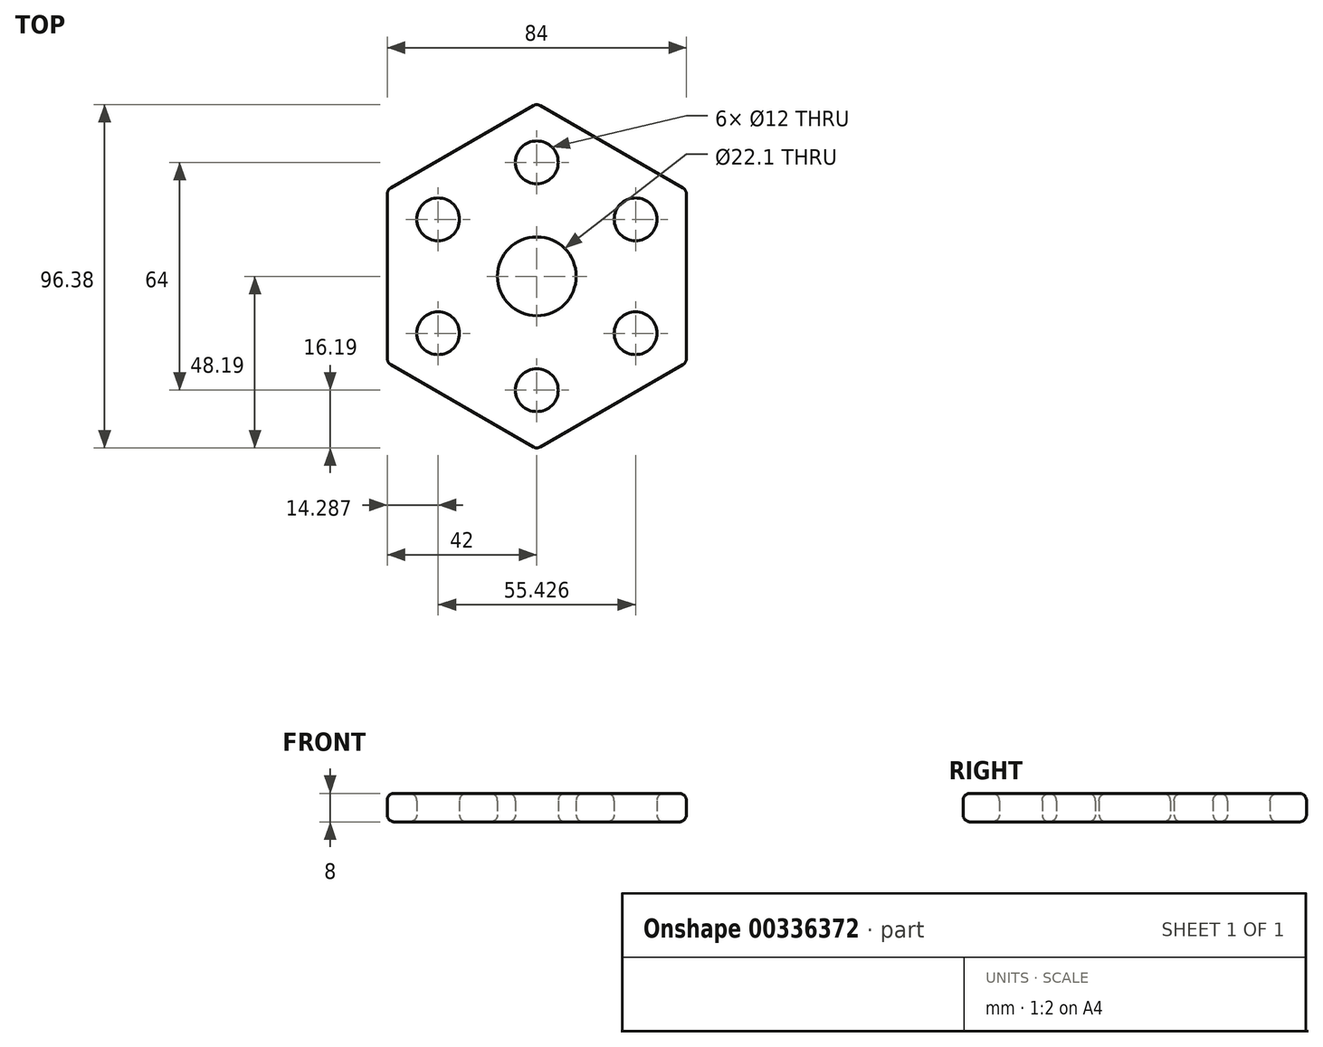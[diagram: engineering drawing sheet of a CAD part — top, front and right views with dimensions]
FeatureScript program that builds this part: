
annotation { "Feature Type Name" : "Feature", "Feature Type Description" : "" }
export const myFeature = defineFeature(function(context is Context, id is Id, definition is map)
    precondition{}
    {
        {
            var Q0;
            Q0=qCreatedBy(makeId("Top.planeOp"),FACE);
            var sketch = newSketch(context, id + "F0", { "sketchPlane" : qUnion([Q0])});
            skCircle(sketch, "E0", {"center": v(0, 0) * mm, "radius": 11.05 * mm});
            skLineSegment(sketch, "E1.0", {"start": v(-42, -24.25) * mm, "end": v(-42, 24.25) * mm});
            skLineSegment(sketch, "E1.1", {"start": v(-42, 24.25) * mm, "end": v(0, 48.5) * mm});
            skLineSegment(sketch, "E1.2", {"start": v(0, 48.5) * mm, "end": v(42, 24.25) * mm});
            skLineSegment(sketch, "E1.3", {"start": v(42, 24.25) * mm, "end": v(42, -24.25) * mm});
            skLineSegment(sketch, "E1.4", {"start": v(42, -24.25) * mm, "end": v(0, -48.5) * mm});
            skLineSegment(sketch, "E1.5", {"start": v(0, -48.5) * mm, "end": v(-42, -24.25) * mm});
            skPoint(sketch, "E1.0.midPoint", {"position": v(-42, 0) * mm});
            skCircle(sketch, "E2", {"center": v(-27.71, 16) * mm, "radius": 6 * mm});
            skCircle(sketch, "E3.MirrorC", {"center": v(-27.71, -16) * mm, "radius": 6 * mm});
            skCircle(sketch, "E4.MirrorC", {"center": v(27.71, 16) * mm, "radius": 6 * mm});
            skCircle(sketch, "E5.MirrorC", {"center": v(27.71, -16) * mm, "radius": 6 * mm});
            skCircle(sketch, "E6.MirrorC", {"center": v(0, 32) * mm, "radius": 6 * mm});
            skCircle(sketch, "E7.MirrorC", {"center": v(0, -32) * mm, "radius": 6 * mm});
            skPoint(sketch, "E8.end.orphan", {"position": v(21, 36.37) * mm});
            skSolve(sketch);
        }
        {
            var Q0;
            Q0 = qSketchRegion(id + "F0", true);
            extrude(context, id + "F1", {"entities" : qUnion([Q0]), "depth" : 8 * mm, "offsetDistance" : 25 * mm});
        }
        {
            var Q0;
            Q0=makeQuery(id+"F1.opExtrude","CAP_FACE",FACE,{"disambiguationData":[OSD([sQuery(id+"F0.wireOp",EDGE,"E0"),sQuery(id+"F0.wireOp",EDGE,"E1.0"),sQuery(id+"F0.wireOp",EDGE,"E1.1"),sQuery(id+"F0.wireOp",EDGE,"E1.2"),sQuery(id+"F0.wireOp",EDGE,"E1.3"),sQuery(id+"F0.wireOp",EDGE,"E1.4"),sQuery(id+"F0.wireOp",EDGE,"E1.5"),sQuery(id+"F0.wireOp",EDGE,"E2"),sQuery(id+"F0.wireOp",EDGE,"E3.MirrorC"),sQuery(id+"F0.wireOp",EDGE,"E4.MirrorC"),sQuery(id+"F0.wireOp",EDGE,"E5.MirrorC"),sQuery(id+"F0.wireOp",EDGE,"E6.MirrorC"),sQuery(id+"F0.wireOp",EDGE,"E7.MirrorC")])],"isStart":false});
            var Q1;
            Q1=makeQuery(id+"F1.opExtrude","CAP_FACE",FACE,{"disambiguationData":[OSD([sQuery(id+"F0.wireOp",EDGE,"E0"),sQuery(id+"F0.wireOp",EDGE,"E1.0"),sQuery(id+"F0.wireOp",EDGE,"E1.1"),sQuery(id+"F0.wireOp",EDGE,"E1.2"),sQuery(id+"F0.wireOp",EDGE,"E1.3"),sQuery(id+"F0.wireOp",EDGE,"E1.4"),sQuery(id+"F0.wireOp",EDGE,"E1.5"),sQuery(id+"F0.wireOp",EDGE,"E2"),sQuery(id+"F0.wireOp",EDGE,"E3.MirrorC"),sQuery(id+"F0.wireOp",EDGE,"E4.MirrorC"),sQuery(id+"F0.wireOp",EDGE,"E5.MirrorC"),sQuery(id+"F0.wireOp",EDGE,"E6.MirrorC"),sQuery(id+"F0.wireOp",EDGE,"E7.MirrorC")])],"isStart":true});
            var Q2;
            Q2=makeQuery(id+"F1.opExtrude","SWEPT_EDGE",EDGE,{"disambiguationData":[OSD([sQuery(id+"F0.wireOp",EDGE,"E1.4"),sQuery(id+"F0.wireOp",EDGE,"E1.5")])]});
            var Q3;
            Q3=makeQuery(id+"F1.opExtrude","SWEPT_EDGE",EDGE,{"disambiguationData":[OSD([sQuery(id+"F0.wireOp",EDGE,"E1.3"),sQuery(id+"F0.wireOp",EDGE,"E1.4")])]});
            var Q4;
            Q4=makeQuery(id+"F1.opExtrude","SWEPT_EDGE",EDGE,{"disambiguationData":[OSD([sQuery(id+"F0.wireOp",EDGE,"E1.2"),sQuery(id+"F0.wireOp",EDGE,"E1.3")])]});
            var Q5;
            Q5=makeQuery(id+"F1.opExtrude","SWEPT_EDGE",EDGE,{"disambiguationData":[OSD([sQuery(id+"F0.wireOp",EDGE,"E1.1"),sQuery(id+"F0.wireOp",EDGE,"E1.2")])]});
            var Q6;
            Q6=makeQuery(id+"F1.opExtrude","SWEPT_EDGE",EDGE,{"disambiguationData":[OSD([sQuery(id+"F0.wireOp",EDGE,"E1.0"),sQuery(id+"F0.wireOp",EDGE,"E1.1")])]});
            var Q7;
            Q7=makeQuery(id+"F1.opExtrude","SWEPT_EDGE",EDGE,{"disambiguationData":[OSD([sQuery(id+"F0.wireOp",EDGE,"E1.0"),sQuery(id+"F0.wireOp",EDGE,"E1.5")])]});
            fillet(context, id + "F2", {"entities" : qUnion([Q0, Q1, Q2, Q3, Q4, Q5, Q6, Q7]), "tangentPropagation" : true, "radius" : 2 * mm, "defaultsChanged" : false, "vertexSettings" : [], "allowEdgeOverflow" : false});
        }
    });
